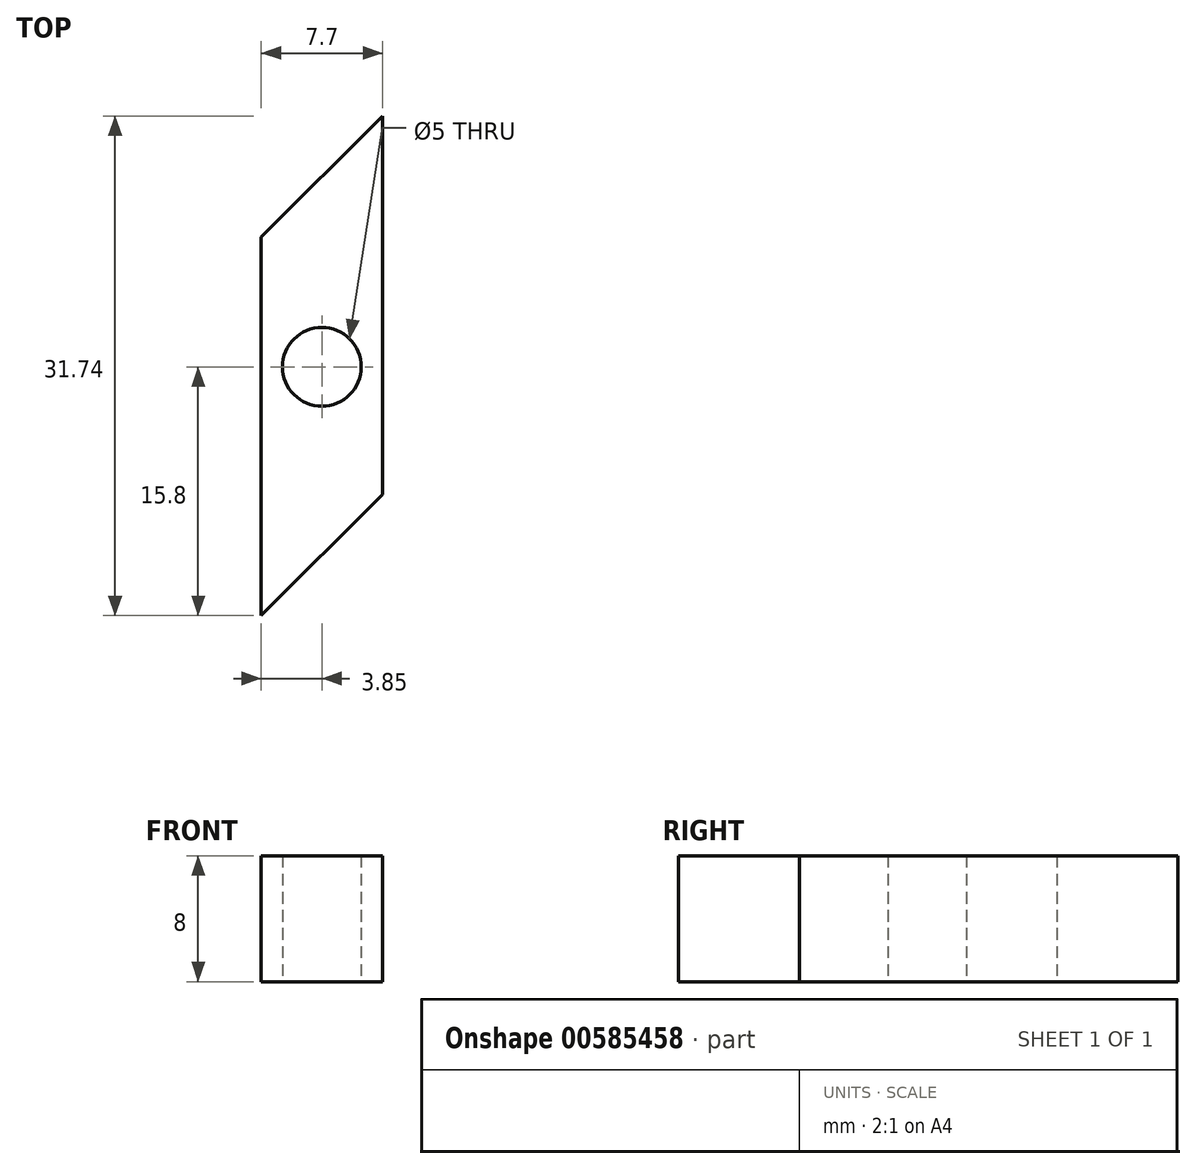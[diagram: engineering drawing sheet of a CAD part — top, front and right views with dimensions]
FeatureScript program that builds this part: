
annotation { "Feature Type Name" : "Feature", "Feature Type Description" : "" }
export const myFeature = defineFeature(function(context is Context, id is Id, definition is map)
    precondition{}
    {
        {
            var Q0;
            Q0=qCreatedBy(makeId("Top.planeOp"),FACE);
            var sketch = newSketch(context, id + "F0", { "sketchPlane" : qUnion([Q0])});
            skLineSegment(sketch, "E0", {"start": v(0, 0) * mm, "end": v(7.7, 7.7) * mm});
            skLineSegment(sketch, "E1", {"start": v(7.7, 7.7) * mm, "end": v(7.7, 31.74) * mm});
            skLineSegment(sketch, "E2", {"start": v(7.7, 31.74) * mm, "end": v(0, 24.04) * mm});
            skLineSegment(sketch, "E3", {"start": v(0, 24.04) * mm, "end": v(0, 0) * mm});
            skCircle(sketch, "E4", {"center": v(3.85, 15.8) * mm, "radius": 2.5 * mm});
            skPoint(sketch, "E5", {"position": v(-3.85, 0) * mm});
            skSolve(sketch);
        }
        {
            var Q0;
            Q0=makeQuery(id+"F0.imprint","IMPRINT",FACE,{"disambiguationData":[TD([[makeQuery(id+"F0.imprint","IMPRINT",EDGE,{"derivedFrom":sQuery(id+"F0.wireOp",EDGE,"E0")}),1.0]])]});
            extrude(context, id + "F1", {"entities" : qUnion([Q0]), "depth" : 8 * mm, "offsetDistance" : 25 * mm});
        }
    });
